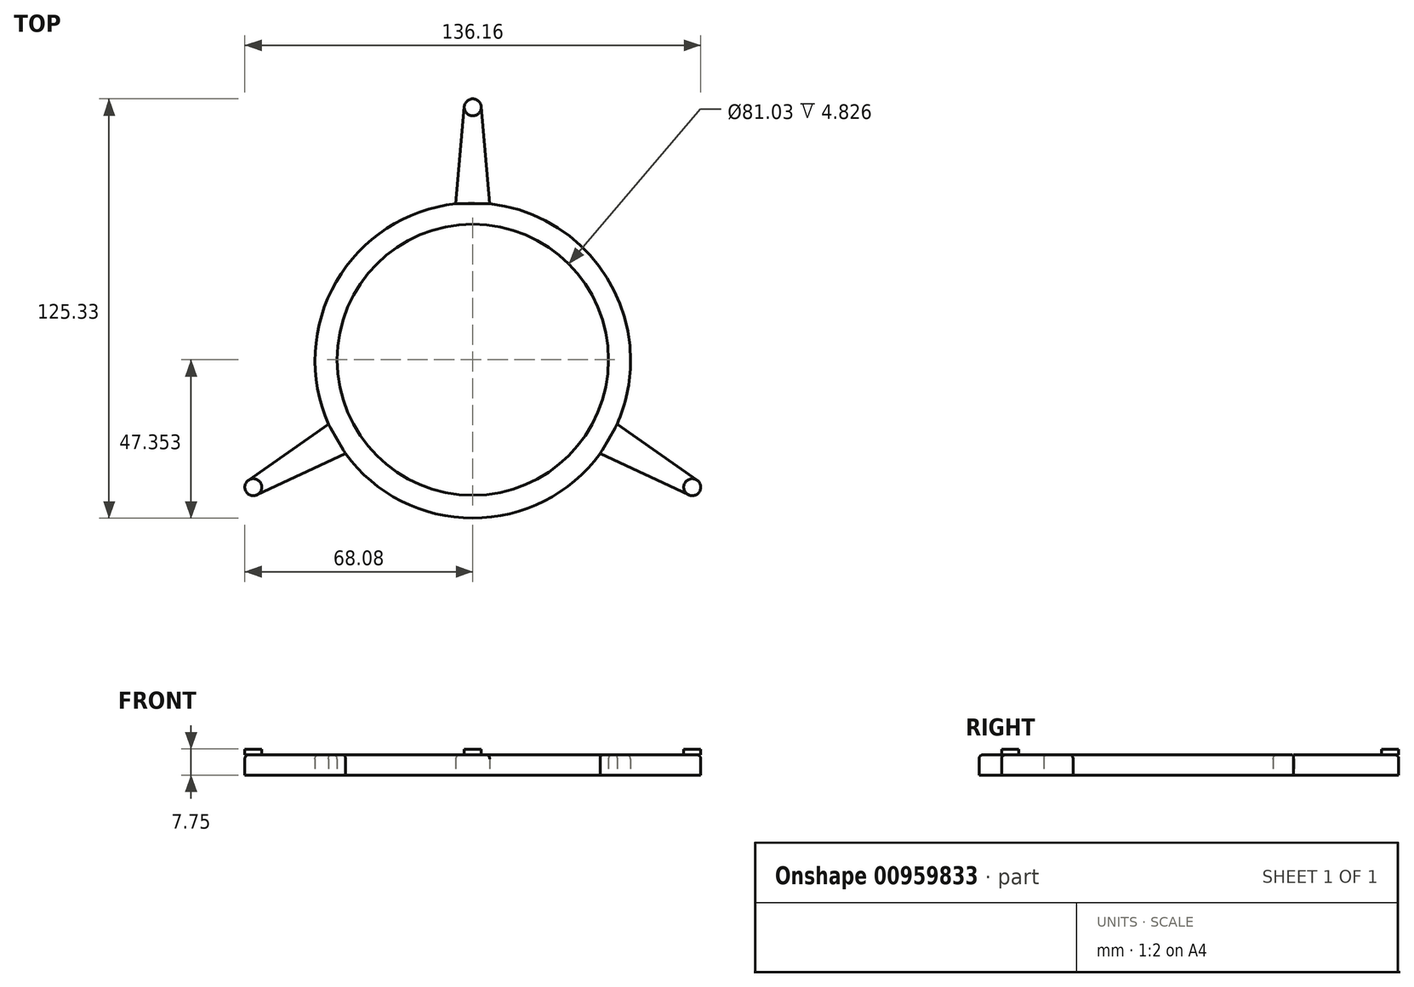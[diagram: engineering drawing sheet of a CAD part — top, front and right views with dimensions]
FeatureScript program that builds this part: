
annotation { "Feature Type Name" : "Feature", "Feature Type Description" : "" }
export const myFeature = defineFeature(function(context is Context, id is Id, definition is map)
    precondition{}
    {
        {
            var Q0;
            Q0=qCreatedBy(makeId("Top.planeOp"),FACE);
            var sketch = newSketch(context, id + "F0", { "sketchPlane" : qUnion([Q0])});
            skCircle(sketch, "E0", {"center": v(0, 0.24) * mm, "radius": 40.51 * mm});
            skCircle(sketch, "E1", {"center": v(0, 0) * mm, "radius": 47.1 * mm});
            skSolve(sketch);
        }
        {
            var Q0;
            Q0 = qSketchRegion(id + "F0", true);
            extrude(context, id + "F1", {"entities" : qUnion([Q0]), "depth" : 6.1 * mm, "offsetDistance" : 25.4 * mm});
        }
        {
            var Q0;
            Q0=makeQuery(id+"F1.opExtrude","CAP_FACE",FACE,{"disambiguationData":[OSD([sQuery(id+"F0.wireOp",EDGE,"E0"),sQuery(id+"F0.wireOp",EDGE,"E1")])],"isStart":true});
            var sketch = newSketch(context, id + "F2", { "sketchPlane" : qUnion([Q0])});
            skLineSegment(sketch, "E2", {"start": v(5.07, -46.83) * mm, "end": v(2.53, -75.9) * mm});
            skLineSegment(sketch, "E3", {"start": v(-5.07, -46.83) * mm, "end": v(-2.53, -75.9) * mm});
            skArc(sketch, "E4", {"start": v(2.53, -75.9) * mm, "mid": v(0, -78.22) * mm, "end": v(-2.53, -75.9) * mm});
            skLineSegment(sketch, "E5", {"start": v(0, -75.68) * mm, "end": v(0, -47.1) * mm, "construction": true});
            skLineSegment(sketch, "E6", {"start": v(5.07, -46.83) * mm, "end": v(-5.07, -46.83) * mm});
            skSolve(sketch);
        }
        {
            var Q0;
            Q0 = qSketchRegion(id + "F2", true);
            var Q1;
            Q1=makeQuery(id+"F1.opExtrude","CAP_FACE",FACE,{"disambiguationData":[OSD([sQuery(id+"F0.wireOp",EDGE,"E0"),sQuery(id+"F0.wireOp",EDGE,"E1")])],"isStart":false});
            extrude(context, id + "F3", {"entities" : qUnion([Q0]), "endBound" : BoundingType.UP_TO_SURFACE, "oppositeDirection" : true, "depth" : 25.4 * mm, "endBoundEntityFace" : qUnion([Q1]), "offsetDistance" : 25.4 * mm});
        }
        {
            var Q0;
            Q0=qCreatedBy(makeId("Right.planeOp"),FACE);
            var sketch = newSketch(context, id + "F4", { "sketchPlane" : qUnion([Q0])});
            skLineSegment(sketch, "E7", {"start": v(0, 0) * mm, "end": v(0, 55.57) * mm, "construction": true});
            skSolve(sketch);
        }
        {
            var Q0;
            Q0=makeQuery(id+"F3.opExtrude","SWEPT_BODY",BODY,{"disambiguationData":[OSD([sQuery(id+"F2.wireOp",EDGE,"E2"),sQuery(id+"F2.wireOp",EDGE,"E3"),sQuery(id+"F2.wireOp",EDGE,"E4"),sQuery(id+"F2.wireOp",EDGE,"E6")])]});
            var Q1;
            Q1=sQuery(id+"F4.wireOp",EDGE,"E7");
            circularPattern(context, id + "F5", {"entities" : qUnion([Q0]), "axis" : qUnion([Q1]), "angle" : 360 * degree, "instanceCount" : 3, "equalSpace" : true});
        }
        {
            var Q0;
            Q0=makeQuery(id+"F5.opPattern","COPY",FACE,{"derivedFrom":makeQuery(id+"F3.opExtrude","CAP_FACE",FACE,{"disambiguationData":[OSD([sQuery(id+"F2.wireOp",EDGE,"E2"),sQuery(id+"F2.wireOp",EDGE,"E3"),sQuery(id+"F2.wireOp",EDGE,"E4"),sQuery(id+"F2.wireOp",EDGE,"E6")])],"isStart":false}),"instanceName":"1"});
            var sketch = newSketch(context, id + "F6", { "sketchPlane" : qUnion([Q0])});
            skCircle(sketch, "E8", {"center": v(-65.54, -37.84) * mm, "radius": 2.54 * mm});
            skCircle(sketch, "E9", {"center": v(65.54, -37.84) * mm, "radius": 2.54 * mm});
            skCircle(sketch, "E10", {"center": v(0, 75.68) * mm, "radius": 2.54 * mm});
            skSolve(sketch);
        }
        {
            var Q0;
            Q0 = qSketchRegion(id + "F6", true);
            extrude(context, id + "F7", {"entities" : qUnion([Q0]), "depth" : 1.65 * mm, "offsetDistance" : 25.4 * mm});
        }
        {
            var Q0;
            Q0=makeQuery(id+"F1.opExtrude","CAP_EDGE",EDGE,{"disambiguationData":[OSD([sQuery(id+"F0.wireOp",EDGE,"E0")])],"isStart":false});
            var Q1;
            Q1=makeQuery(id+"F1.opExtrude","CAP_EDGE",EDGE,{"disambiguationData":[OSD([sQuery(id+"F0.wireOp",EDGE,"E1")])],"isStart":false});
            var Q2;
            Q2=makeQuery(id+"F5.opPattern","COPY",EDGE,{"derivedFrom":makeQuery(id+"F3.opExtrude","CAP_EDGE",EDGE,{"disambiguationData":[OSD([sQuery(id+"F2.wireOp",EDGE,"E3")])],"isStart":false}),"instanceName":"1"});
            var Q3;
            Q3=makeQuery(id+"F5.opPattern","COPY",EDGE,{"derivedFrom":makeQuery(id+"F3.opExtrude","CAP_EDGE",EDGE,{"disambiguationData":[OSD([sQuery(id+"F2.wireOp",EDGE,"E2")])],"isStart":false}),"instanceName":"1"});
            var Q4;
            Q4=makeQuery(id+"F3.opExtrude","CAP_EDGE",EDGE,{"disambiguationData":[OSD([sQuery(id+"F2.wireOp",EDGE,"E2")])],"isStart":false});
            var Q5;
            Q5=makeQuery(id+"F3.opExtrude","CAP_EDGE",EDGE,{"disambiguationData":[OSD([sQuery(id+"F2.wireOp",EDGE,"E3")])],"isStart":false});
            var Q6;
            Q6=makeQuery(id+"F5.opPattern","COPY",EDGE,{"derivedFrom":makeQuery(id+"F3.opExtrude","CAP_EDGE",EDGE,{"disambiguationData":[OSD([sQuery(id+"F2.wireOp",EDGE,"E3")])],"isStart":false}),"instanceName":"2"});
            fillet(context, id + "F8", {"entities" : qUnion([Q0, Q1, Q2, Q3, Q4, Q5, Q6]), "radius" : 1.27 * mm, "tangentPropagation" : true, "allowEdgeOverflow" : false});
        }
    });
